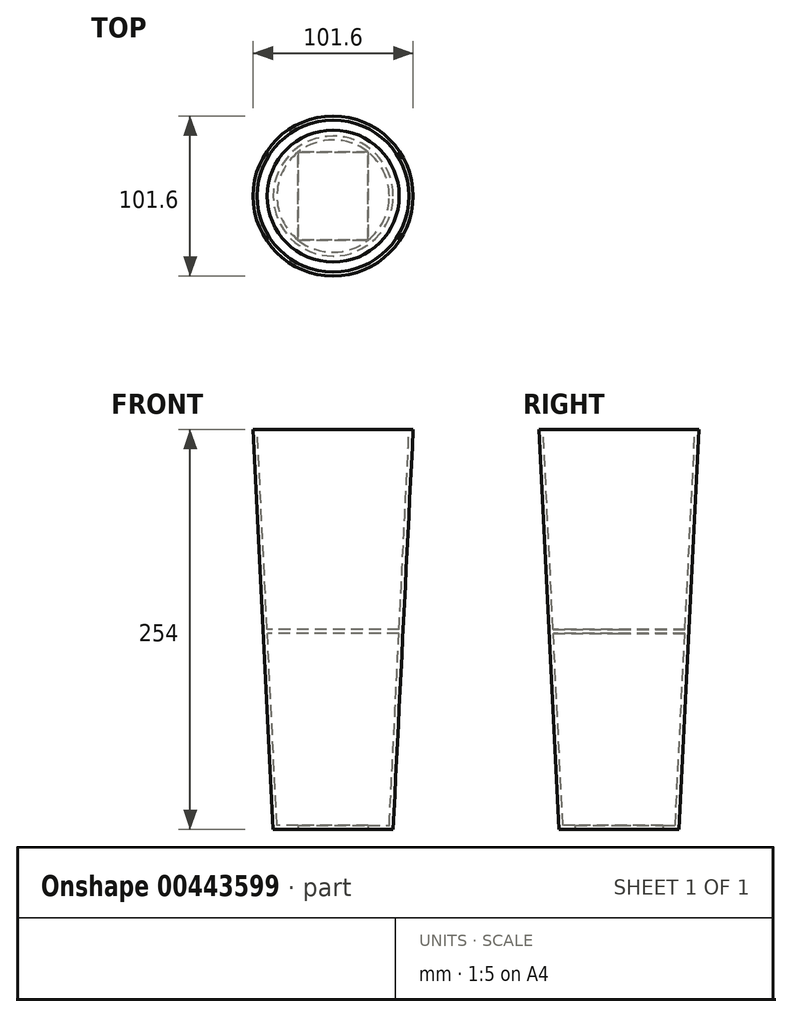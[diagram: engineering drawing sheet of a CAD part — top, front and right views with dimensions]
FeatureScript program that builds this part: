
annotation { "Feature Type Name" : "Feature", "Feature Type Description" : "" }
export const myFeature = defineFeature(function(context is Context, id is Id, definition is map)
    precondition{}
    {
        {
            var Q0;
            Q0=qCreatedBy(makeId("Top.planeOp"),FACE);
            var sketch = newSketch(context, id + "F0", { "sketchPlane" : qUnion([Q0])});
            skCircle(sketch, "E0", {"center": v(0, 0) * mm, "radius": 38.1 * mm});
            skSolve(sketch);
        }
        {
            var Q0;
            Q0=qCreatedBy(makeId("Top.planeOp"),FACE);
            cPlane(context, id + "F1", {"entities" : qUnion([Q0]), "cplaneType" : CPlaneType.OFFSET, "offset" : 254 * mm, "width" : 152.4 * mm, "height" : 152.4 * mm});
        }
        {
            var Q0;
            Q0=qCreatedBy(id+"F1.planeOp",FACE);
            var sketch = newSketch(context, id + "F2", { "sketchPlane" : qUnion([Q0])});
            skCircle(sketch, "E1", {"center": v(0, 0) * mm, "radius": 50.8 * mm});
            skSolve(sketch);
        }
        {
            var Q0;
            Q0 = qSketchRegion(id + "F0", true);
            var Q1;
            Q1 = qSketchRegion(id + "F2", true);
            loft(context, id + "F3", {"sheetProfilesArray" : [{ "sheetProfileEntities" : qUnion([Q0]) }, { "sheetProfileEntities" : qUnion([Q1]) }]});
        }
        {
            var Q0;
            Q0=makeQuery(id+"F3.opLoft","CAP_FACE",FACE,{"disambiguationData":[OSD([makeQuery(id+"F2.imprint","IMPRINT",FACE,{"disambiguationData":[TD([[makeQuery(id+"F2.imprint","IMPRINT",EDGE,{"derivedFrom":sQuery(id+"F2.wireOp",EDGE,"E1")}),1.0]])]})])],"isStart":true});
            shell(context, id + "F4", {"entities" : qUnion([Q0]), "thickness" : 2.54 * mm});
        }
        {
            var Q0;
            Q0=makeQuery(id+"F3.opLoft","CAP_FACE",FACE,{"disambiguationData":[OSD([makeQuery(id+"F0.imprint","IMPRINT",FACE,{"disambiguationData":[TD([[makeQuery(id+"F0.imprint","IMPRINT",EDGE,{"derivedFrom":sQuery(id+"F0.wireOp",EDGE,"E0")}),1.0]])]})])],"isStart":true});
            var sketch = newSketch(context, id + "F5", { "sketchPlane" : qUnion([Q0])});
            skLineSegment(sketch, "E2.bottom", {"start": v(22.23, 27.94) * mm, "end": v(-22.22, 27.94) * mm});
            skLineSegment(sketch, "E2.top", {"start": v(22.23, -27.94) * mm, "end": v(-22.23, -27.94) * mm});
            skLineSegment(sketch, "E2.left", {"start": v(22.23, 27.94) * mm, "end": v(22.23, -27.94) * mm});
            skLineSegment(sketch, "E2.right", {"start": v(-22.22, 27.94) * mm, "end": v(-22.23, -27.94) * mm});
            skPoint(sketch, "E2.middle", {"position": v(0, 0) * mm});
            skSolve(sketch);
        }
        {
            var Q0;
            Q0=makeQuery(id+"F5.imprint","IMPRINT",FACE,{"disambiguationData":[TD([[makeQuery(id+"F5.imprint","IMPRINT",EDGE,{"derivedFrom":sQuery(id+"F5.wireOp",EDGE,"E2.bottom")}),1.0]])]});
            extrude(context, id + "F6", {"entities" : qUnion([Q0]), "operationType" : NewBodyOperationType.REMOVE, "oppositeDirection" : true, "depth" : 25.4 * mm});
        }
        {
            var Q0;
            Q0=qCreatedBy(makeId("Top.planeOp"),FACE);
            cPlane(context, id + "F7", {"entities" : qUnion([Q0]), "cplaneType" : CPlaneType.OFFSET, "offset" : 127 * mm, "width" : 152.4 * mm, "height" : 152.4 * mm});
        }
        {
            var Q0;
            Q0=qCreatedBy(id+"F7.planeOp",FACE);
            var sketch = newSketch(context, id + "F8", { "sketchPlane" : qUnion([Q0])});
            skCircle(sketch, "E3", {"center": v(0, 0) * mm, "radius": 41.91 * mm});
            skSolve(sketch);
        }
        {
            var Q0;
            Q0=makeQuery(id+"F8.imprint","IMPRINT",FACE,{"disambiguationData":[TD([[makeQuery(id+"F8.imprint","IMPRINT",EDGE,{"derivedFrom":sQuery(id+"F8.wireOp",EDGE,"E3")}),1.0]])]});
            extrude(context, id + "F9", {"entities" : qUnion([Q0]), "operationType" : NewBodyOperationType.ADD, "oppositeDirection" : true, "depth" : 2.54 * mm});
        }
    });
